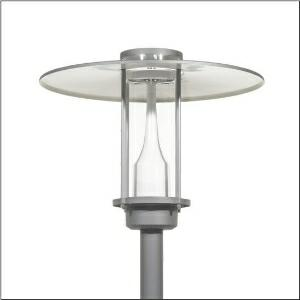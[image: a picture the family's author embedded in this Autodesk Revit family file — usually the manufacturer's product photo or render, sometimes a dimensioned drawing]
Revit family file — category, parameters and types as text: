
# Revit family: city-light_plus_iq___pl1_2s_5xa5275jf14h000022_32ba
name_source: partatom
category: Lighting Fixtures
units: mm (PartAtom-declared; Revit-internal decimal feet)

## family parameters
Cut with Voids When Loaded = No
Host = Face
Light Source = No
Part Type = Normal
Room Calculation Point = No
Round Connector Dimension = Use Diameter
Shared = No

## types (1)
- --- (1 x LED, 2830 lm, 19.3 W, 3000K)
    Apparent Load = 19 VA
    CIE Flux Codes = 23 63 93 97 100
    Color Rendering = 70
    Color Temperature = 3000K
    Default Elevation = 1800 mm
    Description = City-Light Plus iQ, mast luminaire, Module 540 iQ-SR, primary light control with 3 zone facetted reflector, of plastic, silver coated, highly specular, structured, primary optical cover: cover, of PMMA, transparent, light distribution: PL1.2s, light emission: direct distribution, primary light characteristic: symmetric, installation type: post-top, LED, High Power LED, rated luminous flux: 2.830lm, luminous efficacy: 147lm/W, light colour: 730, colour temperature: 3000K, control gear: iQ Street-Remote, control: Street-Remote, Auto-Match, Temp-Guard, Lumen-Switch, Night-Set, Smart-Wire, Light-Fading, Desk-Remote (wireless, voltage-free reading and setting of iQ features in the workshop via application-optimized NFC function/RFID function), optimised constant luminous flux control (CLO 2.0), pre-setting: logarithmic dimming characteristic, mains connection: 230..240V, AC, 50/60Hz, connection cable pre-assembled, cable length: 5,5m, wiring characteristics: H07RN-F, start of lifetime: 19W, end of service life: 21W, reduction: 10W, luminaire housing, upper part, of glass-fibre reinforced polyester, coated, Siteco® metallic grey (DB 702S), diameter: 750mm, height: 590mm, spigot size: d x l = 76 x 70mm (post-top) | with reducer (optional accessory) 60 x 70mm, mounting height: 3..5m, post-top mast mounting element, of diecast aluminium, coated, Siteco® metallic grey (DB 702S), Module 540 iQ-SR, traffic white (RAL 9016), equipment: standard, protection rating (complete): IP65, insulation class (complete): insulation class II (safety insulation), certification: CE, ENEC, VDE, packaging unit: 1 piece

Light Distribution: PL1.2s
    Height = 590 mm
    Lamp = 1 x LED
    Lamp Light Flux = 2830 lm
    Lamp Power = 19.3 W
    Lamp count = 1
    Length = 750 mm
    Luminous efficacy = 147 lm/W
    Manufacturer = Siteco
    ModVariant = No
    Model = 5XA5275JF14H000022
    Number of Poles = 1
    OnlyDefault = Yes
    Power Factor = 1
    Product Name = City-Light Plus iQ | PL1.2s
    Product group = mast luminaire | pylon top
    ProductGroupID = 6100
    Protection Class = Protection class II
    Protection Degree = IP 65
    RLX_Detail_Level = 1
    RLX_Emergency_Light_Flux = 0 lm
    RLX_Emergency_Type = 0
    RLX_Emergency_Type_DB = No
    RlxData = <blob elided: 33269 chars, md5=025d73c3>
    Socket = socket
    Standby Power = 0 W
    System Light Flux = 2830 lm
    System Power = 19 W
    Type Comments = factory setting: luminous flux: 100 % | dim-lin: 254 | 403 mA
    Type Image = l_1006456.jpg
    URL = http://relux.com
    VarID = @adj_145486
    Voltage = 0 V
    Weight = 0.00 kg
    Width = 0 mm  [stored 0 ft]

note: [stored X ft] marks values corroborated as IEEE doubles in the binary element streams (Revit-internal decimal feet)

## geometry (parser evidence)
native form markers: Blend x4, Sweep x10
no freeform markers — native parametric forms only
